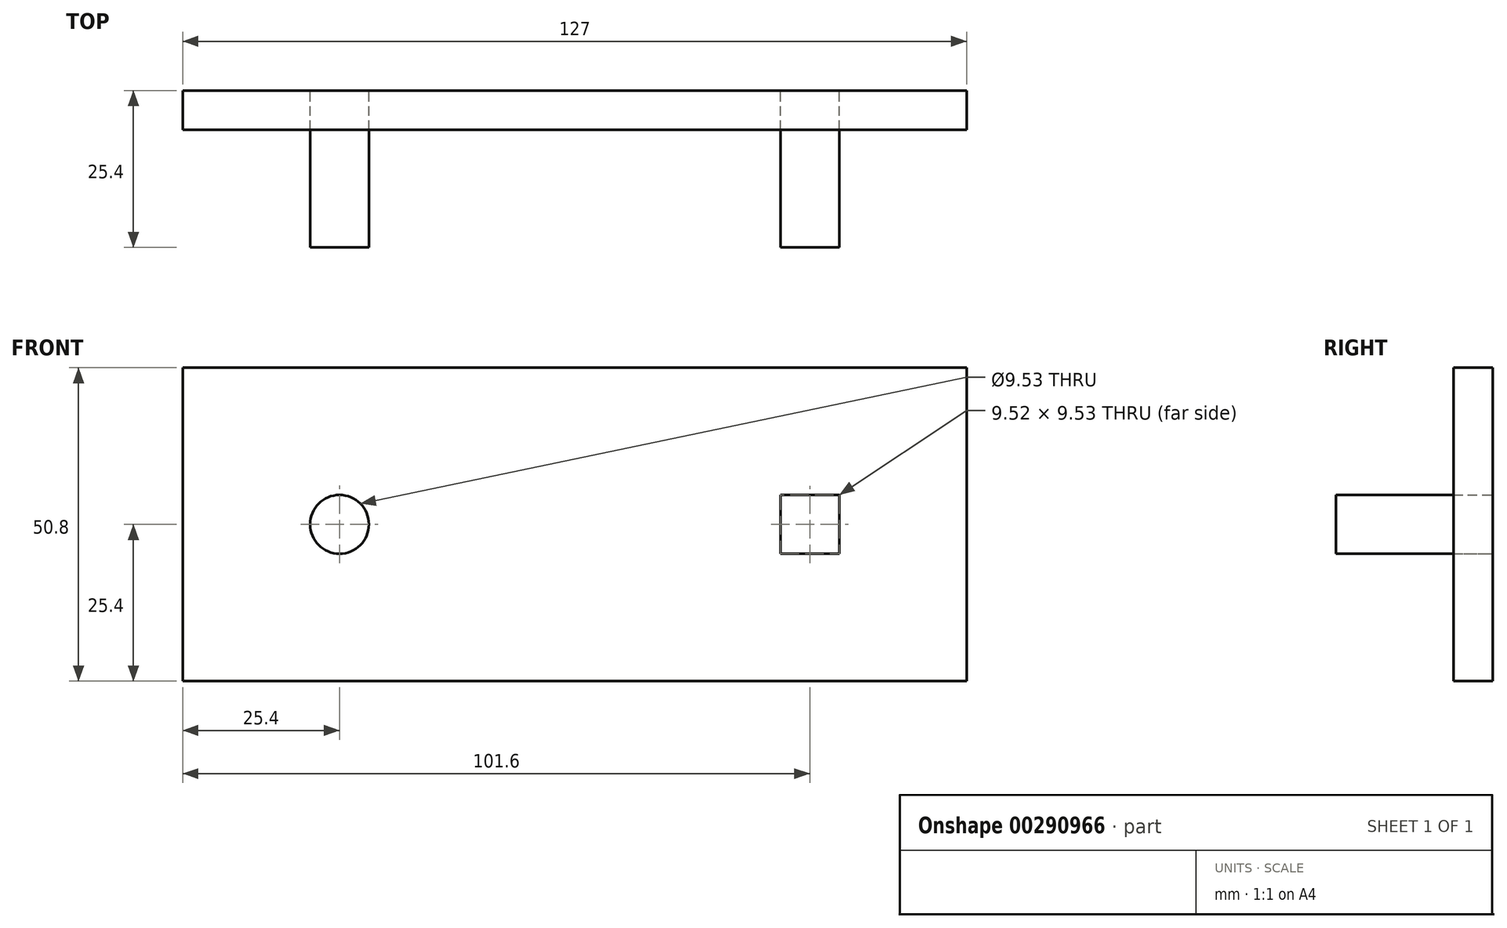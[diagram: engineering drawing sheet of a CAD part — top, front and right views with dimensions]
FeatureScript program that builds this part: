
annotation { "Feature Type Name" : "Feature", "Feature Type Description" : "" }
export const myFeature = defineFeature(function(context is Context, id is Id, definition is map)
    precondition{}
    {
        {
            var Q0;
            Q0=qCreatedBy(makeId("Front.planeOp"),FACE);
            var sketch = newSketch(context, id + "F0", { "sketchPlane" : qUnion([Q0])});
            skLineSegment(sketch, "E0.bottom", {"start": v(-63.5, 25.4) * mm, "end": v(63.5, 25.4) * mm});
            skLineSegment(sketch, "E0.top", {"start": v(-63.5, -25.4) * mm, "end": v(63.5, -25.4) * mm});
            skLineSegment(sketch, "E0.left", {"start": v(-63.5, 25.4) * mm, "end": v(-63.5, -25.4) * mm});
            skLineSegment(sketch, "E0.right", {"start": v(63.5, 25.4) * mm, "end": v(63.5, -25.4) * mm});
            skPoint(sketch, "E0.middle", {"position": v(0, 0) * mm});
            skCircle(sketch, "E1", {"center": v(-38.1, 0) * mm, "radius": 4.76 * mm});
            skLineSegment(sketch, "E2.bottom", {"start": v(42.86, 4.76) * mm, "end": v(33.34, 4.76) * mm});
            skLineSegment(sketch, "E2.top", {"start": v(42.86, -4.76) * mm, "end": v(33.34, -4.76) * mm});
            skLineSegment(sketch, "E2.left", {"start": v(42.86, 4.76) * mm, "end": v(42.86, -4.76) * mm});
            skLineSegment(sketch, "E2.right", {"start": v(33.34, 4.76) * mm, "end": v(33.34, -4.76) * mm});
            skPoint(sketch, "E2.middle", {"position": v(38.1, 0) * mm});
            skSolve(sketch);
        }
        {
            var Q0;
            Q0=makeQuery(id+"F0.imprint","IMPRINT",FACE,{"disambiguationData":[TD([[makeQuery(id+"F0.imprint","IMPRINT",EDGE,{"derivedFrom":sQuery(id+"F0.wireOp",EDGE,"E1")}),1.0]])]});
            var Q1;
            Q1=makeQuery(id+"F0.imprint","IMPRINT",FACE,{"disambiguationData":[TD([[makeQuery(id+"F0.imprint","IMPRINT",EDGE,{"derivedFrom":sQuery(id+"F0.wireOp",EDGE,"E2.bottom")}),1.0]])]});
            extrude(context, id + "F1", {"entities" : qUnion([Q0, Q1]), "depth" : 25.4 * mm});
        }
        {
            var Q0;
            Q0=makeQuery(id+"F0.imprint","IMPRINT",FACE,{"disambiguationData":[TD([[makeQuery(id+"F0.imprint","IMPRINT",EDGE,{"derivedFrom":sQuery(id+"F0.wireOp",EDGE,"E0.bottom")}),-1.0]])]});
            extrude(context, id + "F2", {"entities" : qUnion([Q0]), "depth" : 6.35 * mm});
        }
    });
